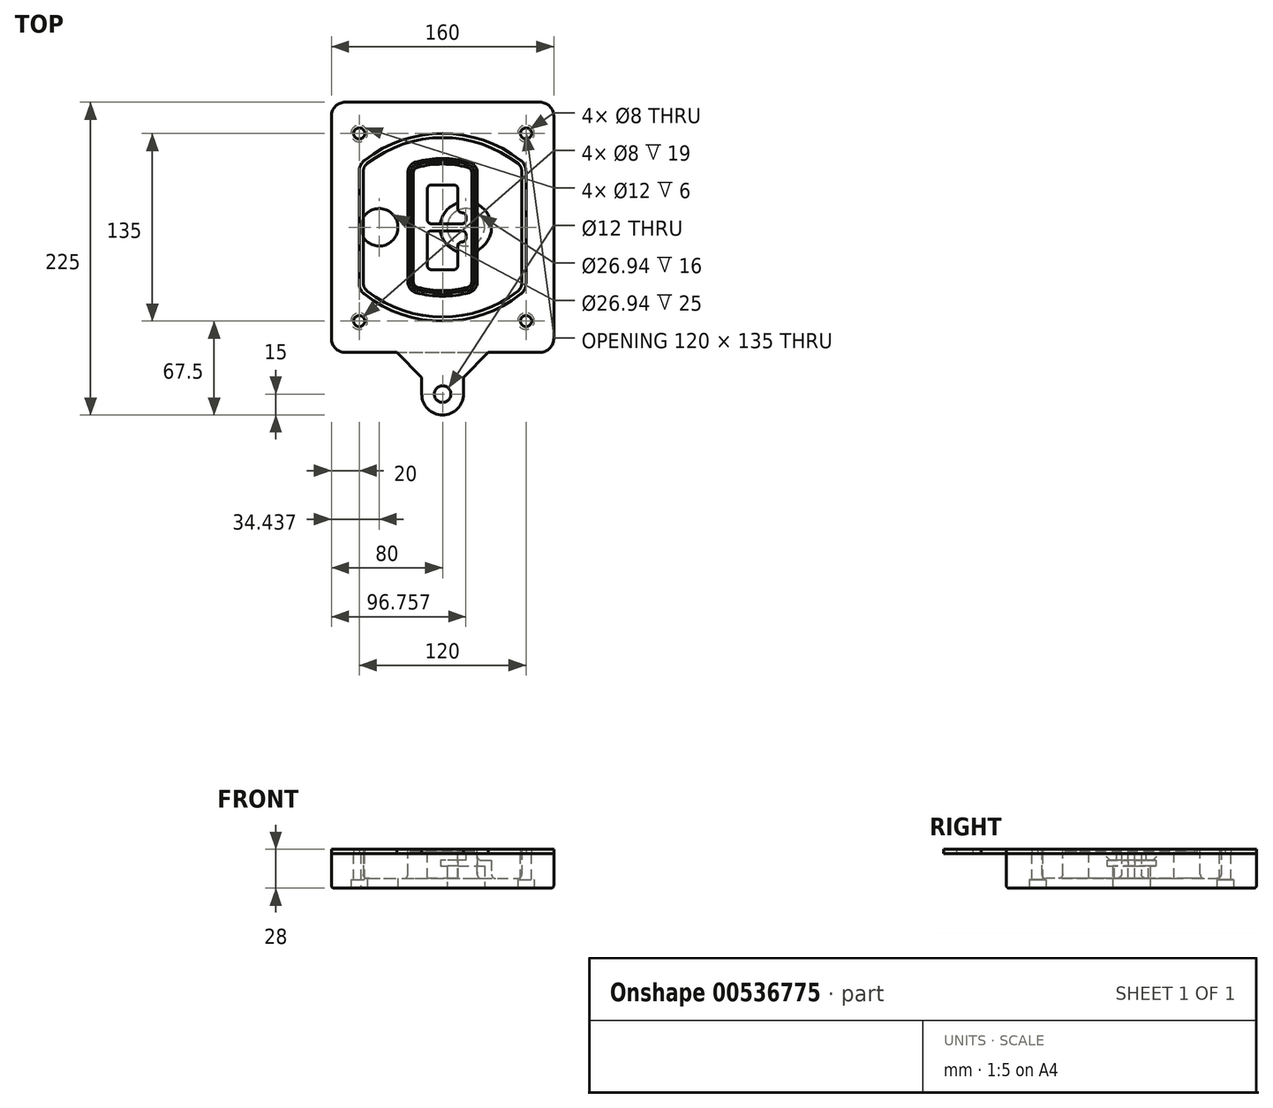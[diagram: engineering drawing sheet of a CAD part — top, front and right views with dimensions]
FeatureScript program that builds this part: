
annotation { "Feature Type Name" : "Feature", "Feature Type Description" : "" }
export const myFeature = defineFeature(function(context is Context, id is Id, definition is map)
    precondition{}
    {
        {
            var Q0;
            Q0=qCreatedBy(makeId("Top.planeOp"),FACE);
            var sketch = newSketch(context, id + "F0", { "sketchPlane" : qUnion([Q0])});
            skPoint(sketch, "E0.rect.middle", {"position": v(0, 0) * mm});
            skLineSegment(sketch, "E1.bottom", {"start": v(-70, -90) * mm, "end": v(70, -90) * mm});
            skLineSegment(sketch, "E1.top", {"start": v(-70, 90) * mm, "end": v(70, 90) * mm});
            skLineSegment(sketch, "E1.left", {"start": v(-80, -80) * mm, "end": v(-80, 80) * mm});
            skLineSegment(sketch, "E1.right", {"start": v(80, -80) * mm, "end": v(80, 80) * mm});
            skLineSegment(sketch, "E2", {"start": v(-80, 90) * mm, "end": v(80, -90) * mm, "construction": true});
            skLineSegment(sketch, "E3", {"start": v(80, 90) * mm, "end": v(-80, -90) * mm, "construction": true});
            skCircle(sketch, "E4", {"center": v(-60, 67.5) * mm, "radius": 4 * mm});
            skCircle(sketch, "E5", {"center": v(60, 67.5) * mm, "radius": 4 * mm});
            skCircle(sketch, "E6", {"center": v(60, -67.5) * mm, "radius": 4 * mm});
            skCircle(sketch, "E7", {"center": v(-60, -67.5) * mm, "radius": 4 * mm});
            skLineSegment(sketch, "E8", {"start": v(-60, 67.5) * mm, "end": v(60, 67.5) * mm, "construction": true});
            skLineSegment(sketch, "E9", {"start": v(60, 67.5) * mm, "end": v(60, -67.5) * mm, "construction": true});
            skLineSegment(sketch, "E10", {"start": v(60, -67.5) * mm, "end": v(-60, -67.5) * mm, "construction": true});
            skLineSegment(sketch, "E11", {"start": v(-60, -67.5) * mm, "end": v(-60, 67.5) * mm, "construction": true});
            skLineSegment(sketch, "E12", {"start": v(-60, 40.3) * mm, "end": v(-60, -40.3) * mm});
            skLineSegment(sketch, "E13", {"start": v(60, 40.3) * mm, "end": v(60, -40.3) * mm});
            skArc(sketch, "E14", {"start": v(56.15, 48.18) * mm, "mid": v(0, 67.5) * mm, "end": v(-56.15, 48.18) * mm});
            skArc(sketch, "E15", {"start": v(-56.15, -48.18) * mm, "mid": v(0, -67.5) * mm, "end": v(56.15, -48.18) * mm});
            skLineSegment(sketch, "E16", {"start": v(-60, 0) * mm, "end": v(60, 0) * mm, "construction": true});
            skPoint(sketch, "E17.visualSharp", {"position": v(-60, -45) * mm});
            skArc(sketch, "E17.filletArc", {"start": v(-60, -40.3) * mm, "mid": v(-58.99, -44.68) * mm, "end": v(-56.15, -48.18) * mm});
            skPoint(sketch, "E18.visualSharp", {"position": v(-60, 45) * mm});
            skArc(sketch, "E18.filletArc", {"start": v(-56.15, 48.18) * mm, "mid": v(-58.99, 44.68) * mm, "end": v(-60, 40.3) * mm});
            skPoint(sketch, "E19.visualSharp", {"position": v(60, 45) * mm});
            skArc(sketch, "E19.filletArc", {"start": v(60, 40.3) * mm, "mid": v(58.99, 44.68) * mm, "end": v(56.15, 48.18) * mm});
            skPoint(sketch, "E20.visualSharp", {"position": v(60, -45) * mm});
            skArc(sketch, "E20.filletArc", {"start": v(56.15, -48.18) * mm, "mid": v(58.99, -44.68) * mm, "end": v(60, -40.3) * mm});
            skPoint(sketch, "E21.visualSharp", {"position": v(-80, 90) * mm});
            skArc(sketch, "E21.filletArc", {"start": v(-70, 90) * mm, "mid": v(-77.07, 87.07) * mm, "end": v(-80, 80) * mm});
            skPoint(sketch, "E22.visualSharp", {"position": v(80, 90) * mm});
            skArc(sketch, "E22.filletArc", {"start": v(80, 80) * mm, "mid": v(77.07, 87.07) * mm, "end": v(70, 90) * mm});
            skPoint(sketch, "E23.visualSharp", {"position": v(80, -90) * mm});
            skArc(sketch, "E23.filletArc", {"start": v(70, -90) * mm, "mid": v(77.07, -87.07) * mm, "end": v(80, -80) * mm});
            skPoint(sketch, "E24.visualSharp", {"position": v(-80, -90) * mm});
            skArc(sketch, "E24.filletArc", {"start": v(-80, -80) * mm, "mid": v(-77.07, -87.07) * mm, "end": v(-70, -90) * mm});
            skArc(sketch, "E25.0", {"start": v(57, 40.3) * mm, "mid": v(56.3, 43.36) * mm, "end": v(54.3, 45.81) * mm});
            skLineSegment(sketch, "E25.1", {"start": v(57, 40.3) * mm, "end": v(57, -40.3) * mm});
            skArc(sketch, "E25.2", {"start": v(54.3, -45.81) * mm, "mid": v(56.3, -43.36) * mm, "end": v(57, -40.3) * mm});
            skArc(sketch, "E25.3", {"start": v(-54.3, -45.81) * mm, "mid": v(0, -64.5) * mm, "end": v(54.3, -45.81) * mm});
            skArc(sketch, "E25.4", {"start": v(-57, -40.3) * mm, "mid": v(-56.3, -43.36) * mm, "end": v(-54.3, -45.81) * mm});
            skArc(sketch, "E25.5", {"start": v(54.3, 45.81) * mm, "mid": v(0, 64.5) * mm, "end": v(-54.3, 45.81) * mm});
            skLineSegment(sketch, "E25.6", {"start": v(-57, 40.3) * mm, "end": v(-57, -40.3) * mm});
            skArc(sketch, "E25.7", {"start": v(-54.3, 45.81) * mm, "mid": v(-56.3, 43.36) * mm, "end": v(-57, 40.3) * mm});
            skArc(sketch, "E26.0", {"start": v(-58.62, 51.33) * mm, "mid": v(-62.58, 46.43) * mm, "end": v(-64, 40.3) * mm});
            skArc(sketch, "E26.1", {"start": v(58.62, 51.33) * mm, "mid": v(0, 71.5) * mm, "end": v(-58.62, 51.33) * mm});
            skArc(sketch, "E26.2", {"start": v(64, 40.3) * mm, "mid": v(62.58, 46.43) * mm, "end": v(58.62, 51.33) * mm});
            skLineSegment(sketch, "E26.3", {"start": v(64, 40.3) * mm, "end": v(64, -40.3) * mm});
            skArc(sketch, "E26.4", {"start": v(58.62, -51.33) * mm, "mid": v(62.58, -46.43) * mm, "end": v(64, -40.3) * mm});
            skLineSegment(sketch, "E26.5", {"start": v(-64, 40.3) * mm, "end": v(-64, -40.3) * mm});
            skArc(sketch, "E26.6", {"start": v(-58.62, -51.33) * mm, "mid": v(0, -71.5) * mm, "end": v(58.62, -51.33) * mm});
            skArc(sketch, "E26.7", {"start": v(-64, -40.3) * mm, "mid": v(-62.58, -46.43) * mm, "end": v(-58.62, -51.33) * mm});
            skSolve(sketch);
        }
        {
            var Q0;
            Q0=makeQuery(id+"F0.imprint","IMPRINT",FACE,{"disambiguationData":[TD([[makeQuery(id+"F0.imprint","IMPRINT",EDGE,{"derivedFrom":sQuery(id+"F0.wireOp",EDGE,"E1.bottom")}),1.0]])]});
            var Q1;
            Q1=makeQuery(id+"F0.imprint","IMPRINT",FACE,{"disambiguationData":[TD([[makeQuery(id+"F0.imprint","IMPRINT",EDGE,{"derivedFrom":sQuery(id+"F0.wireOp",EDGE,"E12")}),1.0]])]});
            var Q2;
            Q2=makeQuery(id+"F0.imprint","IMPRINT",FACE,{"disambiguationData":[TD([[makeQuery(id+"F0.imprint","IMPRINT",EDGE,{"derivedFrom":sQuery(id+"F0.wireOp",EDGE,"E25.0")}),1.0]])]});
            var Q3;
            Q3=makeQuery(id+"F0.imprint","IMPRINT",FACE,{"disambiguationData":[TD([[makeQuery(id+"F0.imprint","IMPRINT",EDGE,{"derivedFrom":sQuery(id+"F0.wireOp",EDGE,"E12")}),-1.0]])]});
            extrude(context, id + "F1", {"entities" : qUnion([Q0, Q1, Q2, Q3]), "oppositeDirection" : true, "depth" : 25 * mm});
        }
        {
            var Q0;
            Q0=makeQuery(id+"F0.imprint","IMPRINT",FACE,{"disambiguationData":[TD([[makeQuery(id+"F0.imprint","IMPRINT",EDGE,{"derivedFrom":sQuery(id+"F0.wireOp",EDGE,"E12")}),1.0]])]});
            extrude(context, id + "F2", {"entities" : qUnion([Q0]), "operationType" : NewBodyOperationType.ADD, "depth" : 3 * mm});
        }
        {
            var Q0;
            Q0=makeQuery(id+"F0.imprint","IMPRINT",FACE,{"disambiguationData":[TD([[makeQuery(id+"F0.imprint","IMPRINT",EDGE,{"derivedFrom":sQuery(id+"F0.wireOp",EDGE,"E25.0")}),1.0]])]});
            extrude(context, id + "F3", {"entities" : qUnion([Q0]), "operationType" : NewBodyOperationType.REMOVE, "oppositeDirection" : true, "depth" : 18 * mm});
        }
        {
            var Q0;
            Q0=makeQuery(id+"F2.opExtrude","CAP_FACE",FACE,{"disambiguationData":[OSD([sQuery(id+"F0.wireOp",EDGE,"E12"),sQuery(id+"F0.wireOp",EDGE,"E13"),sQuery(id+"F0.wireOp",EDGE,"E14"),sQuery(id+"F0.wireOp",EDGE,"E15"),sQuery(id+"F0.wireOp",EDGE,"E17.filletArc"),sQuery(id+"F0.wireOp",EDGE,"E18.filletArc"),sQuery(id+"F0.wireOp",EDGE,"E19.filletArc"),sQuery(id+"F0.wireOp",EDGE,"E20.filletArc"),sQuery(id+"F0.wireOp",EDGE,"E25.0"),sQuery(id+"F0.wireOp",EDGE,"E25.1"),sQuery(id+"F0.wireOp",EDGE,"E25.2"),sQuery(id+"F0.wireOp",EDGE,"E25.3"),sQuery(id+"F0.wireOp",EDGE,"E25.4"),sQuery(id+"F0.wireOp",EDGE,"E25.5"),sQuery(id+"F0.wireOp",EDGE,"E25.6"),sQuery(id+"F0.wireOp",EDGE,"E25.7")])],"isStart":false});
            var sketch = newSketch(context, id + "F4", { "sketchPlane" : qUnion([Q0])});
            skArc(sketch, "E27.0", {"start": v(-19.08, -46.97) * mm, "mid": v(0, -49.5) * mm, "end": v(19.08, -46.97) * mm});
            skArc(sketch, "E28.0", {"start": v(19.08, 46.97) * mm, "mid": v(0, 49.5) * mm, "end": v(-19.08, 46.97) * mm});
            skLineSegment(sketch, "E29", {"start": v(-25, 39.25) * mm, "end": v(-25, -39.25) * mm});
            skLineSegment(sketch, "E30", {"start": v(25, 39.25) * mm, "end": v(25, -39.25) * mm});
            skLineSegment(sketch, "E31", {"start": v(-25, 45.1) * mm, "end": v(25, 45.1) * mm, "construction": true});
            skLineSegment(sketch, "E32", {"start": v(-25, -45.1) * mm, "end": v(25, -45.1) * mm, "construction": true});
            skPoint(sketch, "E33.visualSharp", {"position": v(-25, 45.1) * mm});
            skArc(sketch, "E33.filletArc", {"start": v(-19.08, 46.97) * mm, "mid": v(-23.35, 44.11) * mm, "end": v(-25, 39.25) * mm});
            skPoint(sketch, "E34.visualSharp", {"position": v(25, 45.1) * mm});
            skArc(sketch, "E34.filletArc", {"start": v(25, 39.25) * mm, "mid": v(23.35, 44.11) * mm, "end": v(19.08, 46.97) * mm});
            skPoint(sketch, "E35.visualSharp", {"position": v(25, -45.1) * mm});
            skArc(sketch, "E35.filletArc", {"start": v(19.08, -46.97) * mm, "mid": v(23.35, -44.11) * mm, "end": v(25, -39.25) * mm});
            skPoint(sketch, "E36.visualSharp", {"position": v(-25, -45.1) * mm});
            skArc(sketch, "E36.filletArc", {"start": v(-25, -39.25) * mm, "mid": v(-23.35, -44.11) * mm, "end": v(-19.08, -46.97) * mm});
            skArc(sketch, "E37.0", {"start": v(54.3, 45.81) * mm, "mid": v(0, 64.5) * mm, "end": v(-54.3, 45.81) * mm});
            skArc(sketch, "E37.1", {"start": v(-54.3, 45.81) * mm, "mid": v(-56.3, 43.36) * mm, "end": v(-57, 40.3) * mm});
            skLineSegment(sketch, "E37.2", {"start": v(-57, 40.3) * mm, "end": v(-57, -40.3) * mm});
            skArc(sketch, "E37.3", {"start": v(-57, -40.3) * mm, "mid": v(-56.3, -43.36) * mm, "end": v(-54.3, -45.81) * mm});
            skArc(sketch, "E37.4", {"start": v(-54.3, -45.81) * mm, "mid": v(0, -64.5) * mm, "end": v(54.3, -45.81) * mm});
            skArc(sketch, "E37.5", {"start": v(54.3, -45.81) * mm, "mid": v(56.3, -43.36) * mm, "end": v(57, -40.3) * mm});
            skLineSegment(sketch, "E37.6", {"start": v(57, 40.3) * mm, "end": v(57, -40.3) * mm});
            skArc(sketch, "E37.7", {"start": v(57, 40.3) * mm, "mid": v(56.3, 43.36) * mm, "end": v(54.3, 45.81) * mm});
            skLineSegment(sketch, "E38.0", {"start": v(23, 39.25) * mm, "end": v(23, -39.25) * mm});
            skArc(sketch, "E38.1", {"start": v(18.56, -45.04) * mm, "mid": v(21.76, -42.9) * mm, "end": v(23, -39.25) * mm});
            skArc(sketch, "E38.2", {"start": v(-18.56, -45.04) * mm, "mid": v(0, -47.5) * mm, "end": v(18.56, -45.04) * mm});
            skArc(sketch, "E38.3", {"start": v(-23, -39.25) * mm, "mid": v(-21.76, -42.9) * mm, "end": v(-18.56, -45.04) * mm});
            skLineSegment(sketch, "E38.4", {"start": v(-23, 39.25) * mm, "end": v(-23, -39.25) * mm});
            skArc(sketch, "E38.5", {"start": v(23, 39.25) * mm, "mid": v(21.76, 42.9) * mm, "end": v(18.56, 45.04) * mm});
            skArc(sketch, "E38.6", {"start": v(-18.56, 45.04) * mm, "mid": v(-21.76, 42.9) * mm, "end": v(-23, 39.25) * mm});
            skArc(sketch, "E38.7", {"start": v(18.56, 45.04) * mm, "mid": v(0, 47.5) * mm, "end": v(-18.56, 45.04) * mm});
            skArc(sketch, "E39.0", {"start": v(21, 39.25) * mm, "mid": v(20.18, 41.68) * mm, "end": v(18.04, 43.1) * mm});
            skLineSegment(sketch, "E39.1", {"start": v(21, 39.25) * mm, "end": v(21, -39.25) * mm});
            skArc(sketch, "E39.2", {"start": v(18.04, -43.1) * mm, "mid": v(20.18, -41.68) * mm, "end": v(21, -39.25) * mm});
            skArc(sketch, "E39.3", {"start": v(-18.04, -43.1) * mm, "mid": v(0, -45.5) * mm, "end": v(18.04, -43.1) * mm});
            skArc(sketch, "E39.4", {"start": v(-21, -39.25) * mm, "mid": v(-20.18, -41.68) * mm, "end": v(-18.04, -43.1) * mm});
            skArc(sketch, "E39.5", {"start": v(18.04, 43.1) * mm, "mid": v(0, 45.5) * mm, "end": v(-18.04, 43.1) * mm});
            skLineSegment(sketch, "E39.6", {"start": v(-21, 39.25) * mm, "end": v(-21, -39.25) * mm});
            skArc(sketch, "E39.7", {"start": v(-18.04, 43.1) * mm, "mid": v(-20.18, 41.68) * mm, "end": v(-21, 39.25) * mm});
            skLineSegment(sketch, "E40", {"start": v(-25, 0) * mm, "end": v(25, 0) * mm, "construction": true});
            skLineSegment(sketch, "E41", {"start": v(-11, 5.5) * mm, "end": v(-11, 27.5) * mm});
            skLineSegment(sketch, "E42", {"start": v(-8, 30.5) * mm, "end": v(8, 30.5) * mm});
            skLineSegment(sketch, "E43", {"start": v(11, 27.5) * mm, "end": v(11, 13.5) * mm});
            skLineSegment(sketch, "E44", {"start": v(14, 10.5) * mm, "end": v(14, 10.5) * mm});
            skLineSegment(sketch, "E45", {"start": v(17, 7.5) * mm, "end": v(17, 5.5) * mm});
            skLineSegment(sketch, "E46", {"start": v(14, 2.5) * mm, "end": v(-8, 2.5) * mm});
            skPoint(sketch, "E47.visualSharp", {"position": v(-11, 30.5) * mm});
            skArc(sketch, "E47.filletArc", {"start": v(-8, 30.5) * mm, "mid": v(-10.12, 29.62) * mm, "end": v(-11, 27.5) * mm});
            skPoint(sketch, "E48.visualSharp", {"position": v(11, 30.5) * mm});
            skArc(sketch, "E48.filletArc", {"start": v(11, 27.5) * mm, "mid": v(10.12, 29.62) * mm, "end": v(8, 30.5) * mm});
            skPoint(sketch, "E49.visualSharp", {"position": v(11, 10.5) * mm});
            skArc(sketch, "E49.filletArc", {"start": v(11, 13.5) * mm, "mid": v(11.88, 11.38) * mm, "end": v(14, 10.5) * mm});
            skPoint(sketch, "E50.visualSharp", {"position": v(17, 10.5) * mm});
            skArc(sketch, "E50.filletArc", {"start": v(17, 7.5) * mm, "mid": v(16.12, 9.62) * mm, "end": v(14, 10.5) * mm});
            skPoint(sketch, "E51.visualSharp", {"position": v(17, 2.5) * mm});
            skArc(sketch, "E51.filletArc", {"start": v(14, 2.5) * mm, "mid": v(16.12, 3.38) * mm, "end": v(17, 5.5) * mm});
            skPoint(sketch, "E52.visualSharp", {"position": v(-11, 2.5) * mm});
            skArc(sketch, "E52.filletArc", {"start": v(-11, 5.5) * mm, "mid": v(-10.12, 3.38) * mm, "end": v(-8, 2.5) * mm});
            skLineSegment(sketch, "E53.0.MirrorCS", {"start": v(14, -2.5) * mm, "end": v(-8, -2.5) * mm});
            skArc(sketch, "E54.0.MirrorCS", {"start": v(-11, -5.5) * mm, "mid": v(-10.12, -3.38) * mm, "end": v(-8, -2.5) * mm});
            skLineSegment(sketch, "E55.0.MirrorCS", {"start": v(-11, -5.5) * mm, "end": v(-11, -27.5) * mm});
            skArc(sketch, "E56.0.MirrorCS", {"start": v(-8, -30.5) * mm, "mid": v(-10.12, -29.62) * mm, "end": v(-11, -27.5) * mm});
            skLineSegment(sketch, "E57.0.MirrorCS", {"start": v(-8, -30.5) * mm, "end": v(8, -30.5) * mm});
            skArc(sketch, "E58.0.MirrorCS", {"start": v(11, -27.5) * mm, "mid": v(10.12, -29.62) * mm, "end": v(8, -30.5) * mm});
            skLineSegment(sketch, "E59.0.MirrorCS", {"start": v(11, -27.5) * mm, "end": v(11, -13.5) * mm});
            skArc(sketch, "E60.0.MirrorCS", {"start": v(11, -13.5) * mm, "mid": v(11.88, -11.38) * mm, "end": v(14, -10.5) * mm});
            skArc(sketch, "E61.0.MirrorCS", {"start": v(17, -7.5) * mm, "mid": v(16.12, -9.62) * mm, "end": v(14, -10.5) * mm});
            skLineSegment(sketch, "E62.0.MirrorCS", {"start": v(17, -7.5) * mm, "end": v(17, -5.5) * mm});
            skArc(sketch, "E63.0.MirrorCS", {"start": v(14, -2.5) * mm, "mid": v(16.12, -3.38) * mm, "end": v(17, -5.5) * mm});
            skSolve(sketch);
        }
        {
            var Q0;
            Q0=makeQuery(id+"F4.imprint","IMPRINT",FACE,{"disambiguationData":[TD([[makeQuery(id+"F4.imprint","IMPRINT",EDGE,{"derivedFrom":sQuery(id+"F4.wireOp",EDGE,"E27.0")}),1.0]])]});
            var Q1;
            Q1=makeQuery(id+"F4.imprint","IMPRINT",FACE,{"disambiguationData":[TD([[makeQuery(id+"F4.imprint","IMPRINT",EDGE,{"derivedFrom":sQuery(id+"F4.wireOp",EDGE,"E38.0")}),-1.0]])]});
            var Q2;
            Q2=makeQuery(id+"F4.imprint","IMPRINT",FACE,{"disambiguationData":[TD([[makeQuery(id+"F4.imprint","IMPRINT",EDGE,{"derivedFrom":sQuery(id+"F4.wireOp",EDGE,"E39.0")}),1.0]])]});
            extrude(context, id + "F5", {"entities" : qUnion([Q0, Q1, Q2]), "operationType" : NewBodyOperationType.ADD, "endBound" : BoundingType.UP_TO_NEXT, "oppositeDirection" : true, "depth" : 25 * mm});
        }
        {
            var Q0;
            Q0=makeQuery(id+"F4.imprint","IMPRINT",FACE,{"disambiguationData":[TD([[makeQuery(id+"F4.imprint","IMPRINT",EDGE,{"derivedFrom":sQuery(id+"F4.wireOp",EDGE,"E38.0")}),-1.0]])]});
            extrude(context, id + "F6", {"entities" : qUnion([Q0]), "operationType" : NewBodyOperationType.REMOVE, "oppositeDirection" : true, "depth" : 2 * mm});
        }
        {
            var Q0;
            Q0=makeQuery(id+"F1.opExtrude","CAP_FACE",FACE,{"disambiguationData":[OSD([sQuery(id+"F0.wireOp",EDGE,"E1.bottom"),sQuery(id+"F0.wireOp",EDGE,"E1.top"),sQuery(id+"F0.wireOp",EDGE,"E1.left"),sQuery(id+"F0.wireOp",EDGE,"E1.right"),sQuery(id+"F0.wireOp",EDGE,"E4"),sQuery(id+"F0.wireOp",EDGE,"E5"),sQuery(id+"F0.wireOp",EDGE,"E6"),sQuery(id+"F0.wireOp",EDGE,"E7"),sQuery(id+"F0.wireOp",EDGE,"E21.filletArc"),sQuery(id+"F0.wireOp",EDGE,"E22.filletArc"),sQuery(id+"F0.wireOp",EDGE,"E23.filletArc"),sQuery(id+"F0.wireOp",EDGE,"E24.filletArc")])],"isStart":false});
            var sketch = newSketch(context, id + "F7", { "sketchPlane" : qUnion([Q0])});
            skCircle(sketch, "E64", {"center": v(16.76, 0) * mm, "radius": 13.47 * mm});
            skCircle(sketch, "E65", {"center": v(-45.56, 0) * mm, "radius": 13.47 * mm});
            skLineSegment(sketch, "E66", {"start": v(80, 0) * mm, "end": v(-80, 0) * mm});
            skCircle(sketch, "E67", {"center": v(16.76, 0) * mm, "radius": 18.47 * mm});
            skCircle(sketch, "E68", {"center": v(60, -67.5) * mm, "radius": 6 * mm});
            skCircle(sketch, "E69", {"center": v(-60, -67.5) * mm, "radius": 6 * mm});
            skCircle(sketch, "E70", {"center": v(-60, 67.5) * mm, "radius": 6 * mm});
            skCircle(sketch, "E71", {"center": v(60, 67.5) * mm, "radius": 6 * mm});
            skSolve(sketch);
        }
        {
            var Q0;
            {var subQ1=sQuery(id+"F7.wireOp",EDGE,"E66");var subQ4=sQuery(id+"F7.wireOp",EDGE,"E64");var subQ6=makeQuery(id+"F7.imprint","INTERSECT",VERTEX,{"disambiguationData":[OD(0.0)],"derivedFrom":[subQ4,subQ1]});Q0=makeQuery(id+"F7.imprint","IMPRINT",FACE,{"disambiguationData":[TD([[makeQuery(id+"F7.imprint","IMPRINT",EDGE,{"disambiguationData":[TD([[subQ6,-1.0]])],"derivedFrom":subQ4}),-1.0]])]});}
            var Q1;
            {var subQ0=sQuery(id+"F7.wireOp",EDGE,"E66");var subQ1=sQuery(id+"F7.wireOp",EDGE,"E64");var subQ3=makeQuery(id+"F7.imprint","INTERSECT",VERTEX,{"disambiguationData":[OD(0.0)],"derivedFrom":[subQ1,subQ0]});Q1=makeQuery(id+"F7.imprint","IMPRINT",FACE,{"disambiguationData":[TD([[makeQuery(id+"F7.imprint","IMPRINT",EDGE,{"disambiguationData":[TD([[subQ3,-1.0]])],"derivedFrom":subQ1}),1.0]])]});}
            var Q2;
            {var subQ0=sQuery(id+"F7.wireOp",EDGE,"E66");var subQ1=sQuery(id+"F7.wireOp",EDGE,"E64");var subQ3=makeQuery(id+"F7.imprint","INTERSECT",VERTEX,{"disambiguationData":[OD(0.0)],"derivedFrom":[subQ1,subQ0]});Q2=makeQuery(id+"F7.imprint","IMPRINT",FACE,{"disambiguationData":[TD([[makeQuery(id+"F7.imprint","IMPRINT",EDGE,{"disambiguationData":[TD([[subQ3,1.0]])],"derivedFrom":subQ1}),1.0]])]});}
            var Q3;
            {var subQ1=sQuery(id+"F7.wireOp",EDGE,"E66");var subQ4=sQuery(id+"F7.wireOp",EDGE,"E64");var subQ6=makeQuery(id+"F7.imprint","INTERSECT",VERTEX,{"disambiguationData":[OD(0.0)],"derivedFrom":[subQ4,subQ1]});Q3=makeQuery(id+"F7.imprint","IMPRINT",FACE,{"disambiguationData":[TD([[makeQuery(id+"F7.imprint","IMPRINT",EDGE,{"disambiguationData":[TD([[subQ6,1.0]])],"derivedFrom":subQ4}),-1.0]])]});}
            extrude(context, id + "F8", {"entities" : qUnion([Q0, Q1, Q2, Q3]), "operationType" : NewBodyOperationType.ADD, "oppositeDirection" : true, "depth" : 20 * mm, "offsetDistance" : 25 * mm});
        }
        {
            var Q0;
            {var subQ0=sQuery(id+"F7.wireOp",EDGE,"E66");var subQ1=sQuery(id+"F7.wireOp",EDGE,"E64");var subQ3=makeQuery(id+"F7.imprint","INTERSECT",VERTEX,{"disambiguationData":[OD(0.0)],"derivedFrom":[subQ1,subQ0]});Q0=makeQuery(id+"F7.imprint","IMPRINT",FACE,{"disambiguationData":[TD([[makeQuery(id+"F7.imprint","IMPRINT",EDGE,{"disambiguationData":[TD([[subQ3,-1.0]])],"derivedFrom":subQ1}),1.0]])]});}
            var Q1;
            {var subQ0=sQuery(id+"F7.wireOp",EDGE,"E66");var subQ1=sQuery(id+"F7.wireOp",EDGE,"E64");var subQ3=makeQuery(id+"F7.imprint","INTERSECT",VERTEX,{"disambiguationData":[OD(0.0)],"derivedFrom":[subQ1,subQ0]});Q1=makeQuery(id+"F7.imprint","IMPRINT",FACE,{"disambiguationData":[TD([[makeQuery(id+"F7.imprint","IMPRINT",EDGE,{"disambiguationData":[TD([[subQ3,1.0]])],"derivedFrom":subQ1}),1.0]])]});}
            extrude(context, id + "F9", {"entities" : qUnion([Q0, Q1]), "operationType" : NewBodyOperationType.REMOVE, "oppositeDirection" : true, "depth" : 16 * mm});
        }
        {
            var Q0;
            {var subQ0=sQuery(id+"F7.wireOp",EDGE,"E66");var subQ1=sQuery(id+"F7.wireOp",EDGE,"E65");var subQ3=makeQuery(id+"F7.imprint","INTERSECT",VERTEX,{"disambiguationData":[OD(0.0)],"derivedFrom":[subQ1,subQ0]});Q0=makeQuery(id+"F7.imprint","IMPRINT",FACE,{"disambiguationData":[TD([[makeQuery(id+"F7.imprint","IMPRINT",EDGE,{"disambiguationData":[TD([[subQ3,-1.0]])],"derivedFrom":subQ1}),1.0]])]});}
            var Q1;
            {var subQ0=sQuery(id+"F7.wireOp",EDGE,"E66");var subQ1=sQuery(id+"F7.wireOp",EDGE,"E65");var subQ3=makeQuery(id+"F7.imprint","INTERSECT",VERTEX,{"disambiguationData":[OD(0.0)],"derivedFrom":[subQ1,subQ0]});Q1=makeQuery(id+"F7.imprint","IMPRINT",FACE,{"disambiguationData":[TD([[makeQuery(id+"F7.imprint","IMPRINT",EDGE,{"disambiguationData":[TD([[subQ3,1.0]])],"derivedFrom":subQ1}),1.0]])]});}
            extrude(context, id + "F10", {"entities" : qUnion([Q0, Q1]), "operationType" : NewBodyOperationType.REMOVE, "oppositeDirection" : true, "depth" : 25 * mm});
        }
        {
            var Q0;
            Q0=makeQuery(id+"F7.imprint","IMPRINT",FACE,{"disambiguationData":[TD([[makeQuery(id+"F7.imprint","IMPRINT",EDGE,{"derivedFrom":sQuery(id+"F7.wireOp",EDGE,"E68")}),1.0]])]});
            var Q1;
            Q1=makeQuery(id+"F7.imprint","IMPRINT",FACE,{"disambiguationData":[TD([[makeQuery(id+"F7.imprint","IMPRINT",EDGE,{"derivedFrom":makeQuery(id+"F1.opExtrude","CAP_EDGE",EDGE,{"disambiguationData":[OSD([sQuery(id+"F0.wireOp",EDGE,"E5")])],"isStart":false})}),-1.0]])]});
            var Q2;
            Q2=makeQuery(id+"F7.imprint","IMPRINT",FACE,{"disambiguationData":[TD([[makeQuery(id+"F7.imprint","IMPRINT",EDGE,{"derivedFrom":sQuery(id+"F7.wireOp",EDGE,"E69")}),1.0]])]});
            var Q3;
            Q3=makeQuery(id+"F7.imprint","IMPRINT",FACE,{"disambiguationData":[TD([[makeQuery(id+"F7.imprint","IMPRINT",EDGE,{"derivedFrom":makeQuery(id+"F1.opExtrude","CAP_EDGE",EDGE,{"disambiguationData":[OSD([sQuery(id+"F0.wireOp",EDGE,"E4")])],"isStart":false})}),-1.0]])]});
            var Q4;
            Q4=makeQuery(id+"F7.imprint","IMPRINT",FACE,{"disambiguationData":[TD([[makeQuery(id+"F7.imprint","IMPRINT",EDGE,{"derivedFrom":sQuery(id+"F7.wireOp",EDGE,"E70")}),1.0]])]});
            var Q5;
            Q5=makeQuery(id+"F7.imprint","IMPRINT",FACE,{"disambiguationData":[TD([[makeQuery(id+"F7.imprint","IMPRINT",EDGE,{"derivedFrom":makeQuery(id+"F1.opExtrude","CAP_EDGE",EDGE,{"disambiguationData":[OSD([sQuery(id+"F0.wireOp",EDGE,"E7")])],"isStart":false})}),-1.0]])]});
            var Q6;
            Q6=makeQuery(id+"F7.imprint","IMPRINT",FACE,{"disambiguationData":[TD([[makeQuery(id+"F7.imprint","IMPRINT",EDGE,{"derivedFrom":sQuery(id+"F7.wireOp",EDGE,"E71")}),1.0]])]});
            var Q7;
            Q7=makeQuery(id+"F7.imprint","IMPRINT",FACE,{"disambiguationData":[TD([[makeQuery(id+"F7.imprint","IMPRINT",EDGE,{"derivedFrom":makeQuery(id+"F1.opExtrude","CAP_EDGE",EDGE,{"disambiguationData":[OSD([sQuery(id+"F0.wireOp",EDGE,"E6")])],"isStart":false})}),-1.0]])]});
            extrude(context, id + "F11", {"entities" : qUnion([Q0, Q1, Q2, Q3, Q4, Q5, Q6, Q7]), "operationType" : NewBodyOperationType.REMOVE, "oppositeDirection" : true, "depth" : 6 * mm});
        }
        {
            var Q0;
            Q0=makeQuery(id+"F9.boolean.opBoolean","COPY",FACE,{"derivedFrom":makeQuery(id+"F9.opExtrude","CAP_FACE",FACE,{"disambiguationData":[OSD([sQuery(id+"F7.wireOp",EDGE,"E64")])],"isStart":false})});
            var sketch = newSketch(context, id + "F12", { "sketchPlane" : qUnion([Q0])});
            skArc(sketch, "E72.0", {"start": v(11, 17.55) * mm, "mid": v(2.57, 11.82) * mm, "end": v(-1.54, 2.5) * mm});
            skArc(sketch, "E72.1", {"start": v(-1.54, -2.5) * mm, "mid": v(2.57, -11.82) * mm, "end": v(11, -17.55) * mm});
            skLineSegment(sketch, "E73", {"start": v(-1.54, -2.5) * mm, "end": v(14, -2.5) * mm});
            skLineSegment(sketch, "E74.0", {"start": v(14, 2.5) * mm, "end": v(-1.54, 2.5) * mm});
            skArc(sketch, "E74.1", {"start": v(14, 2.5) * mm, "mid": v(16.12, 3.38) * mm, "end": v(17, 5.5) * mm});
            skLineSegment(sketch, "E74.2", {"start": v(17, 7.5) * mm, "end": v(17, 5.5) * mm});
            skArc(sketch, "E74.3", {"start": v(17, 7.5) * mm, "mid": v(16.12, 9.62) * mm, "end": v(14, 10.5) * mm});
            skArc(sketch, "E74.4", {"start": v(11, 13.5) * mm, "mid": v(11.88, 11.38) * mm, "end": v(14, 10.5) * mm});
            skLineSegment(sketch, "E74.5", {"start": v(11, 17.55) * mm, "end": v(11, 13.5) * mm});
            skLineSegment(sketch, "E74.7", {"start": v(14, -2.5) * mm, "end": v(-1.54, -2.5) * mm});
            skArc(sketch, "E74.8", {"start": v(14, -2.5) * mm, "mid": v(16.12, -3.38) * mm, "end": v(17, -5.5) * mm});
            skLineSegment(sketch, "E74.9", {"start": v(17, -7.5) * mm, "end": v(17, -5.5) * mm});
            skArc(sketch, "E74.10", {"start": v(17, -7.5) * mm, "mid": v(16.12, -9.62) * mm, "end": v(14, -10.5) * mm});
            skArc(sketch, "E74.11", {"start": v(11, -13.5) * mm, "mid": v(11.88, -11.38) * mm, "end": v(14, -10.5) * mm});
            skLineSegment(sketch, "E74.12", {"start": v(11, -17.55) * mm, "end": v(11, -13.5) * mm});
            skPoint(sketch, "E75.orphan", {"position": v(11, -27.5) * mm});
            skPoint(sketch, "E76.orphan", {"position": v(-8, -2.5) * mm});
            skPoint(sketch, "E77.orphan", {"position": v(-8, 2.5) * mm});
            skPoint(sketch, "E78.orphan", {"position": v(11, 27.5) * mm});
            skSolve(sketch);
        }
        {
            var Q0;
            {var subQ7=sQuery(id+"F12.wireOp",EDGE,"E72.0");var subQ14=sQuery(id+"F12.wireOp",EDGE,"E72.1");var subQ16=sQuery(id+"F12.wireOp",EDGE,"E74.1");var subQ18=sQuery(id+"F12.wireOp",EDGE,"E74.8");Q0=qUnion([makeQuery(id+"F12.imprint","IMPRINT",FACE,{"disambiguationData":[TD([[makeQuery(id+"F12.imprint","IMPRINT",EDGE,{"derivedFrom":subQ7}),1.0]])]}),makeQuery(id+"F12.imprint","IMPRINT",FACE,{"disambiguationData":[TD([[makeQuery(id+"F12.imprint","IMPRINT",EDGE,{"derivedFrom":subQ14}),1.0]])]}),makeQuery(id+"F12.imprint","IMPRINT",FACE,{"disambiguationData":[TD([[makeQuery(id+"F12.imprint","IMPRINT",EDGE,{"derivedFrom":subQ16}),1.0]])]}),makeQuery(id+"F12.imprint","IMPRINT",FACE,{"disambiguationData":[TD([[makeQuery(id+"F12.imprint","IMPRINT",EDGE,{"derivedFrom":subQ18}),-1.0]])]})]);}
            var Q1;
            Q1=makeQuery(id+"F5.boolean.opBoolean","SPLIT",FACE,{"disambiguationData":[TD([makeQuery(id+"F5.opExtrude","SWEPT_FACE",FACE,{"disambiguationData":[OSD([sQuery(id+"F4.wireOp",EDGE,"E41")])]})])],"derivedFrom":makeQuery(id+"F3.boolean.opBoolean","COPY",FACE,{"derivedFrom":makeQuery(id+"F3.opExtrude","CAP_FACE",FACE,{"disambiguationData":[OSD([sQuery(id+"F0.wireOp",EDGE,"E25.0"),sQuery(id+"F0.wireOp",EDGE,"E25.1"),sQuery(id+"F0.wireOp",EDGE,"E25.2"),sQuery(id+"F0.wireOp",EDGE,"E25.3"),sQuery(id+"F0.wireOp",EDGE,"E25.4"),sQuery(id+"F0.wireOp",EDGE,"E25.5"),sQuery(id+"F0.wireOp",EDGE,"E25.6"),sQuery(id+"F0.wireOp",EDGE,"E25.7")])],"isStart":false})})});
            extrude(context, id + "F13", {"entities" : qUnion([Q0]), "operationType" : NewBodyOperationType.REMOVE, "endBound" : BoundingType.UP_TO_SURFACE, "endBoundEntityFace" : qUnion([Q1]), "depth" : 25 * mm});
        }
        {
            var Q0;
            Q0=makeQuery(id+"F3.boolean.opBoolean","COPY",EDGE,{"derivedFrom":makeQuery(id+"F3.opExtrude","CAP_EDGE",EDGE,{"disambiguationData":[OSD([sQuery(id+"F0.wireOp",EDGE,"E25.6")])],"isStart":false})});
            var Q1;
            Q1=makeQuery(id+"F8.boolean.opBoolean","INTERSECT",EDGE,{"derivedFrom":[makeQuery(id+"F5.opExtrude","SWEPT_FACE",FACE,{"disambiguationData":[OSD([sQuery(id+"F4.wireOp",EDGE,"E30")])]}),makeQuery(id+"F8.opExtrude","CAP_FACE",FACE,{"disambiguationData":[OSD([sQuery(id+"F7.wireOp",EDGE,"E67")])],"isStart":false})]});
            var Q2;
            Q2=makeQuery(id+"F8.boolean.opBoolean","INTERSECT",EDGE,{"disambiguationData":[OD(1.0)],"derivedFrom":[makeQuery(id+"F5.opExtrude","SWEPT_FACE",FACE,{"disambiguationData":[OSD([sQuery(id+"F4.wireOp",EDGE,"E30")])]}),makeQuery(id+"F8.opExtrude","SWEPT_FACE",FACE,{"disambiguationData":[OSD([sQuery(id+"F7.wireOp",EDGE,"E67")])]})]});
            var Q3;
            {var subQ0=sQuery(id+"F4.wireOp",EDGE,"E30");Q3=makeQuery(id+"F8.boolean.opBoolean","SPLIT",EDGE,{"disambiguationData":[TD([makeQuery(id+"F5.opExtrude","SWEPT_FACE",FACE,{"disambiguationData":[OSD([sQuery(id+"F4.wireOp",EDGE,"E35.filletArc")])]})])],"derivedFrom":makeQuery(id+"F5.opExtrude","CAP_EDGE",EDGE,{"disambiguationData":[OSD([subQ0])],"isStart":false})});}
            var Q4;
            {var subQ0=sQuery(id+"F0.wireOp",EDGE,"E25.7");var subQ1=sQuery(id+"F0.wireOp",EDGE,"E25.1");var subQ2=sQuery(id+"F0.wireOp",EDGE,"E25.6");var subQ3=sQuery(id+"F0.wireOp",EDGE,"E25.5");var subQ4=sQuery(id+"F0.wireOp",EDGE,"E25.4");var subQ5=sQuery(id+"F0.wireOp",EDGE,"E25.0");var subQ6=sQuery(id+"F0.wireOp",EDGE,"E25.2");var subQ7=sQuery(id+"F0.wireOp",EDGE,"E25.3");Q4=makeQuery(id+"F8.boolean.opBoolean","INTERSECT",EDGE,{"derivedFrom":[makeQuery(id+"F5.boolean.opBoolean","SPLIT",FACE,{"disambiguationData":[TD([makeQuery(id+"F2.opExtrude","SWEPT_FACE",FACE,{"disambiguationData":[OSD([subQ5])]})])],"derivedFrom":makeQuery(id+"F3.boolean.opBoolean","COPY",FACE,{"derivedFrom":makeQuery(id+"F3.opExtrude","CAP_FACE",FACE,{"disambiguationData":[OSD([subQ5,subQ1,subQ6,subQ7,subQ4,subQ3,subQ2,subQ0])],"isStart":false})})}),makeQuery(id+"F8.opExtrude","SWEPT_FACE",FACE,{"disambiguationData":[OSD([sQuery(id+"F7.wireOp",EDGE,"E67")])]})]});}
            var Q5;
            Q5=makeQuery(id+"F8.boolean.opBoolean","INTERSECT",EDGE,{"disambiguationData":[OD(0.0)],"derivedFrom":[makeQuery(id+"F5.opExtrude","SWEPT_FACE",FACE,{"disambiguationData":[OSD([sQuery(id+"F4.wireOp",EDGE,"E30")])]}),makeQuery(id+"F8.opExtrude","SWEPT_FACE",FACE,{"disambiguationData":[OSD([sQuery(id+"F7.wireOp",EDGE,"E67")])]})]});
            fillet(context, id + "F14", {"entities" : qUnion([Q0, Q1, Q2, Q3, Q4, Q5]), "radius" : 3 * mm, "tangentPropagation" : true, "allowEdgeOverflow" : false});
        }
        {
            var Q0;
            Q0=makeQuery(id+"F1.opExtrude","CAP_EDGE",EDGE,{"disambiguationData":[OSD([sQuery(id+"F0.wireOp",EDGE,"E1.bottom")])],"isStart":false});
            fillet(context, id + "F15", {"entities" : qUnion([Q0]), "radius" : 2 * mm, "tangentPropagation" : true, "allowEdgeOverflow" : false});
        }
        {
            var Q0;
            {var subQ0=sQuery(id+"F0.wireOp",EDGE,"E21.filletArc");var subQ1=sQuery(id+"F0.wireOp",EDGE,"E7");var subQ2=sQuery(id+"F0.wireOp",EDGE,"E6");var subQ3=sQuery(id+"F0.wireOp",EDGE,"E5");var subQ4=sQuery(id+"F0.wireOp",EDGE,"E4");var subQ5=sQuery(id+"F0.wireOp",EDGE,"E22.filletArc");var subQ6=sQuery(id+"F0.wireOp",EDGE,"E1.bottom");var subQ7=sQuery(id+"F0.wireOp",EDGE,"E1.right");var subQ8=sQuery(id+"F0.wireOp",EDGE,"E1.top");var subQ9=sQuery(id+"F0.wireOp",EDGE,"E1.left");var subQ10=sQuery(id+"F0.wireOp",EDGE,"E23.filletArc");var subQ11=sQuery(id+"F0.wireOp",EDGE,"E24.filletArc");Q0=makeQuery(id+"F2.boolean.opBoolean","SPLIT",FACE,{"disambiguationData":[TD([makeQuery(id+"F1.opExtrude","SWEPT_FACE",FACE,{"disambiguationData":[OSD([subQ6])]})])],"derivedFrom":makeQuery(id+"F1.opExtrude","CAP_FACE",FACE,{"disambiguationData":[OSD([subQ6,subQ8,subQ9,subQ7,subQ4,subQ3,subQ2,subQ1,subQ0,subQ5,subQ10,subQ11])],"isStart":true})});}
            var sketch = newSketch(context, id + "F16", { "sketchPlane" : qUnion([Q0])});
            skLineSegment(sketch, "E79", {"start": v(-33, 90) * mm, "end": v(-15, 108) * mm});
            skLineSegment(sketch, "E80", {"start": v(33, 90) * mm, "end": v(15, 108) * mm});
            skLineSegment(sketch, "E81", {"start": v(-15, 108) * mm, "end": v(-15, 120) * mm});
            skLineSegment(sketch, "E82", {"start": v(15, 108) * mm, "end": v(15, 120) * mm});
            skArc(sketch, "E83", {"start": v(15, 120) * mm, "mid": v(0, 135) * mm, "end": v(-15, 120) * mm});
            skCircle(sketch, "E84", {"center": v(0, 120) * mm, "radius": 6 * mm});
            skLineSegment(sketch, "E85", {"start": v(0, 120) * mm, "end": v(0, 90) * mm, "construction": true});
            skLineSegment(sketch, "E86", {"start": v(-80, 0) * mm, "end": v(80, 0) * mm, "construction": true});
            skArc(sketch, "E87.MirrorCS", {"start": v(-15, 120) * mm, "mid": v(0, 135) * mm, "end": v(15, 120) * mm});
            skLineSegment(sketch, "E88.MirrorCS", {"start": v(-33, -90) * mm, "end": v(-15, -108) * mm});
            skLineSegment(sketch, "E89.MirrorCS", {"start": v(-15, -108) * mm, "end": v(-15, -120) * mm});
            skArc(sketch, "E90.MirrorCS", {"start": v(15, -120) * mm, "mid": v(0, -135) * mm, "end": v(-15, -120) * mm});
            skCircle(sketch, "E91.MirrorC", {"center": v(0, -120) * mm, "radius": 6 * mm});
            skLineSegment(sketch, "E92.MirrorCS", {"start": v(0, -120) * mm, "end": v(0, -90) * mm, "construction": true});
            skLineSegment(sketch, "E93.MirrorCS", {"start": v(33, -90) * mm, "end": v(15, -108) * mm});
            skLineSegment(sketch, "E94.MirrorCS", {"start": v(15, -108) * mm, "end": v(15, -120) * mm});
            skSolve(sketch);
        }
        {
            var Q0;
            Q0=makeQuery(id+"F16.imprint","IMPRINT",FACE,{"disambiguationData":[TD([[makeQuery(id+"F16.imprint","IMPRINT",EDGE,{"derivedFrom":sQuery(id+"F16.wireOp",EDGE,"E87.MirrorCS")}),-1.0]])]});
            var Q1;
            Q1=makeQuery(id+"F16.imprint","IMPRINT",FACE,{"disambiguationData":[TD([[makeQuery(id+"F16.imprint","IMPRINT",EDGE,{"derivedFrom":makeQuery(id+"F1.opExtrude","CAP_EDGE",EDGE,{"disambiguationData":[OSD([sQuery(id+"F0.wireOp",EDGE,"E1.left")])],"isStart":true})}),-1.0]])]});
            var Q2;
            {var subQ0=sQuery(id+"F16.wireOp",EDGE,"E88.MirrorCS");Q2=makeQuery(id+"F16.imprint","IMPRINT",FACE,{"disambiguationData":[TD([[makeQuery(id+"F16.imprint","IMPRINT",EDGE,{"derivedFrom":subQ0}),1.0]])]});}
            var Q3;
            Q3=makeQuery(id+"F2.opExtrude","CAP_FACE",FACE,{"disambiguationData":[OSD([sQuery(id+"F0.wireOp",EDGE,"E12"),sQuery(id+"F0.wireOp",EDGE,"E13"),sQuery(id+"F0.wireOp",EDGE,"E14"),sQuery(id+"F0.wireOp",EDGE,"E15"),sQuery(id+"F0.wireOp",EDGE,"E17.filletArc"),sQuery(id+"F0.wireOp",EDGE,"E18.filletArc"),sQuery(id+"F0.wireOp",EDGE,"E19.filletArc"),sQuery(id+"F0.wireOp",EDGE,"E20.filletArc"),sQuery(id+"F0.wireOp",EDGE,"E25.0"),sQuery(id+"F0.wireOp",EDGE,"E25.1"),sQuery(id+"F0.wireOp",EDGE,"E25.2"),sQuery(id+"F0.wireOp",EDGE,"E25.3"),sQuery(id+"F0.wireOp",EDGE,"E25.4"),sQuery(id+"F0.wireOp",EDGE,"E25.5"),sQuery(id+"F0.wireOp",EDGE,"E25.6"),sQuery(id+"F0.wireOp",EDGE,"E25.7")])],"isStart":false});
            extrude(context, id + "F17", {"entities" : qUnion([Q0, Q1, Q2]), "endBound" : BoundingType.UP_TO_SURFACE, "depth" : 25 * mm, "endBoundEntityFace" : qUnion([Q3]), "offsetDistance" : 25 * mm});
        }
    });
